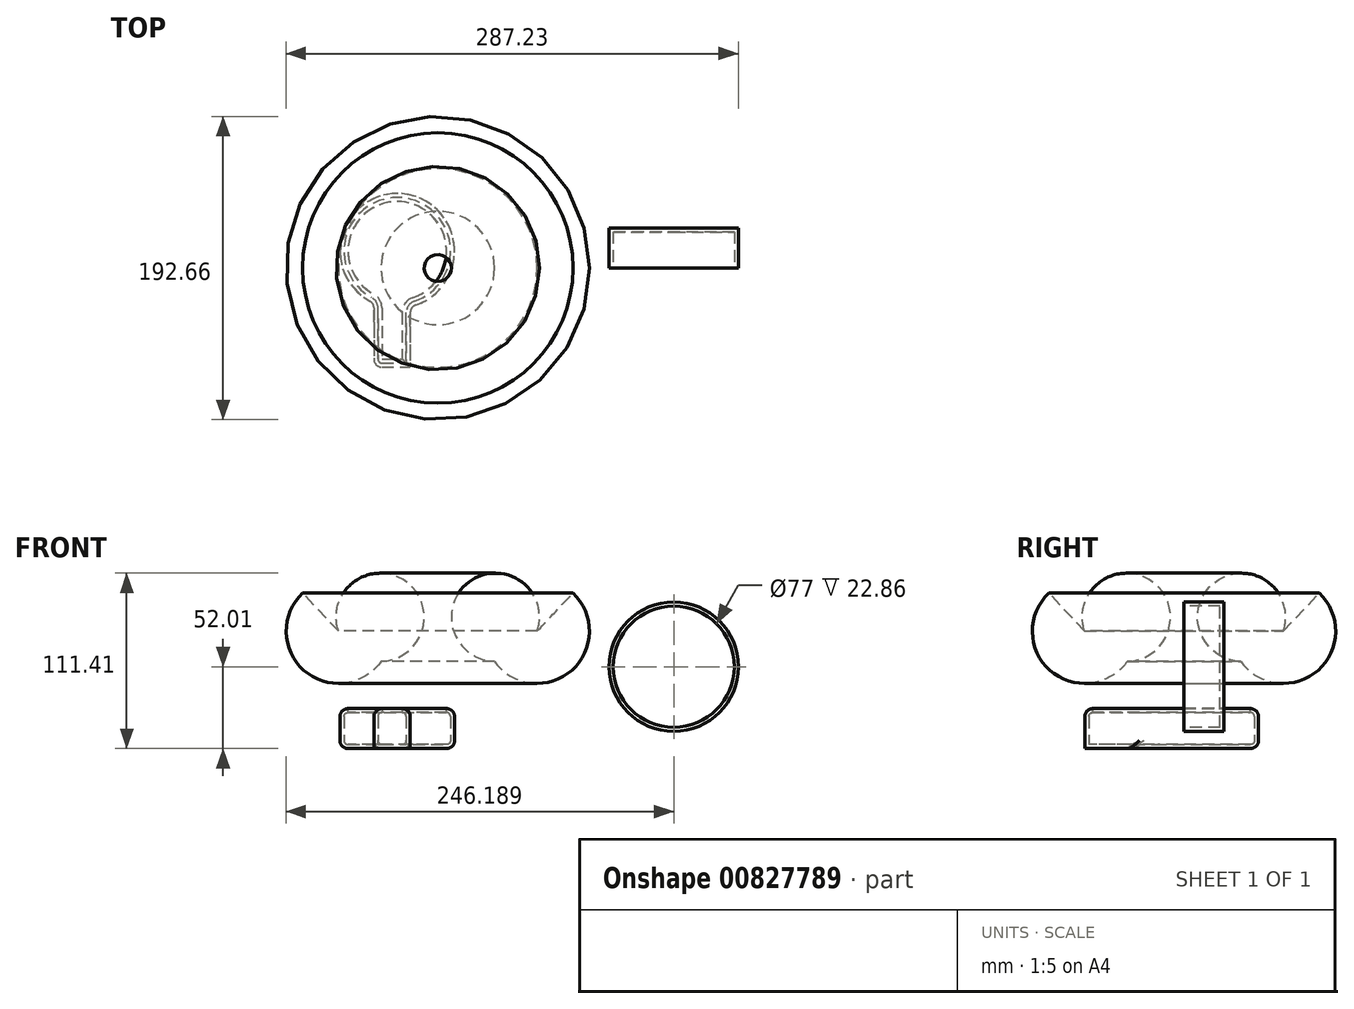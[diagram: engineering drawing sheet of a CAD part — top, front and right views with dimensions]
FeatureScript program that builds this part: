
annotation { "Feature Type Name" : "Feature", "Feature Type Description" : "" }
export const myFeature = defineFeature(function(context is Context, id is Id, definition is map)
    precondition{}
    {
        {
            var Q0;
            Q0=qCreatedBy(makeId("Top.planeOp"),FACE);
            var sketch = newSketch(context, id + "F0", { "sketchPlane" : qUnion([Q0])});
            skArc(sketch, "E0", {"start": v(-126.6, -24.5) * mm, "mid": v(-131.4, 47.12) * mm, "end": v(-149.63, -22.3) * mm});
            skLineSegment(sketch, "E1.top", {"start": v(-149.63, -62.98) * mm, "end": v(-126.6, -62.98) * mm});
            skLineSegment(sketch, "E1.left", {"start": v(-149.63, -16.53) * mm, "end": v(-149.63, -62.98) * mm});
            skLineSegment(sketch, "E1.right", {"start": v(-126.6, -16.53) * mm, "end": v(-126.6, -62.98) * mm});
            skSolve(sketch);
        }
        {
            var Q0;
            Q0 = qSketchRegion(id + "F0", true);
            extrude(context, id + "F1", {"entities" : qUnion([Q0]), "depth" : 25.4 * mm, "offsetDistance" : 25.4 * mm});
        }
        {
            var Q0;
            Q0=qCreatedBy(makeId("Front.planeOp"),FACE);
            var sketch = newSketch(context, id + "F2", { "sketchPlane" : qUnion([Q0])});
            skCircle(sketch, "E2", {"center": v(40.77, 52) * mm, "radius": 41.04 * mm});
            skSolve(sketch);
        }
        {
            var Q0;
            Q0 = qSketchRegion(id + "F2", true);
            extrude(context, id + "F3", {"entities" : qUnion([Q0]), "oppositeDirection" : true, "depth" : 25.4 * mm, "offsetDistance" : 25.4 * mm});
        }
        {
            var Q0;
            Q0=qCreatedBy(makeId("Front.planeOp"),FACE);
            var sketch = newSketch(context, id + "F4", { "sketchPlane" : qUnion([Q0])});
            skArc(sketch, "E3", {"start": v(-73.1, 55.45) * mm, "mid": v(-24.2, 49.51) * mm, "end": v(-23.22, 98.78) * mm});
            skArc(sketch, "E4", {"start": v(-45.97, 74.58) * mm, "mid": v(-88.64, 106.3) * mm, "end": v(-73.1, 55.45) * mm});
            skLineSegment(sketch, "E5", {"start": v(-45.97, 74.58) * mm, "end": v(-23.22, 98.78) * mm});
            skLineSegment(sketch, "E6", {"start": v(-109.1, 128.24) * mm, "end": v(-109.1, 38.15) * mm});
            skSolve(sketch);
        }
        {
            var Q0;
            Q0 = qSketchRegion(id + "F4", true);
            var Q1;
            Q1=sQuery(id+"F4.wireOp",EDGE,"E6");
            revolve(context, id + "F5", {"surfaceOperationType" : NewSurfaceOperationType.NEW, "entities" : qUnion([Q0]), "axis" : qUnion([Q1]), "revolveType" : RevolveType.FULL});
        }
        {
            var Q0;
            Q0=makeQuery(id+"F3.opExtrude","CAP_FACE",FACE,{"disambiguationData":[OSD([sQuery(id+"F2.wireOp",EDGE,"E2")])],"isStart":true});
            shell(context, id + "F6", {"entities" : qUnion([Q0]), "thickness" : 2.54 * mm});
        }
        {
            var Q0;
            Q0=makeQuery(id+"F1.opExtrude","CAP_FACE",FACE,{"disambiguationData":[OSD([sQuery(id+"F0.wireOp",EDGE,"E0"),sQuery(id+"F0.wireOp",EDGE,"E1.top"),sQuery(id+"F0.wireOp",EDGE,"E1.left"),sQuery(id+"F0.wireOp",EDGE,"E1.right")])],"isStart":false});
            var Q1;
            Q1=makeQuery(id+"F1.opExtrude","CAP_EDGE",EDGE,{"disambiguationData":[OSD([sQuery(id+"F0.wireOp",EDGE,"E0")])],"isStart":true});
            var Q2;
            Q2=makeQuery(id+"F1.opExtrude","SWEPT_EDGE",EDGE,{"disambiguationData":[OSD([sQuery(id+"F0.wireOp",EDGE,"E0"),sQuery(id+"F0.wireOp",EDGE,"E1.right")])]});
            var Q3;
            Q3=makeQuery(id+"F1.opExtrude","SWEPT_EDGE",EDGE,{"disambiguationData":[OSD([sQuery(id+"F0.wireOp",EDGE,"E1.top"),sQuery(id+"F0.wireOp",EDGE,"E1.left")])]});
            var Q4;
            Q4=makeQuery(id+"F1.opExtrude","SWEPT_EDGE",EDGE,{"disambiguationData":[OSD([sQuery(id+"F0.wireOp",EDGE,"E0"),sQuery(id+"F0.wireOp",EDGE,"E1.left")])]});
            var Q5;
            Q5=makeQuery(id+"F1.opExtrude","SWEPT_FACE",FACE,{"disambiguationData":[OSD([sQuery(id+"F0.wireOp",EDGE,"E0")])]});
            fillet(context, id + "F7", {"entities" : qUnion([Q0, Q1, Q2, Q3, Q4, Q5]), "radius" : 5.08 * mm, "tangentPropagation" : true, "allowEdgeOverflow" : false});
        }
        {
            var Q0;
            Q0=makeQuery(id+"F1.opExtrude","CAP_FACE",FACE,{"disambiguationData":[OSD([sQuery(id+"F0.wireOp",EDGE,"E0"),sQuery(id+"F0.wireOp",EDGE,"E1.top"),sQuery(id+"F0.wireOp",EDGE,"E1.left"),sQuery(id+"F0.wireOp",EDGE,"E1.right")])],"isStart":false});
            shell(context, id + "F8", {"entities" : qUnion([Q0]), "thickness" : 2.54 * mm});
        }
    });
